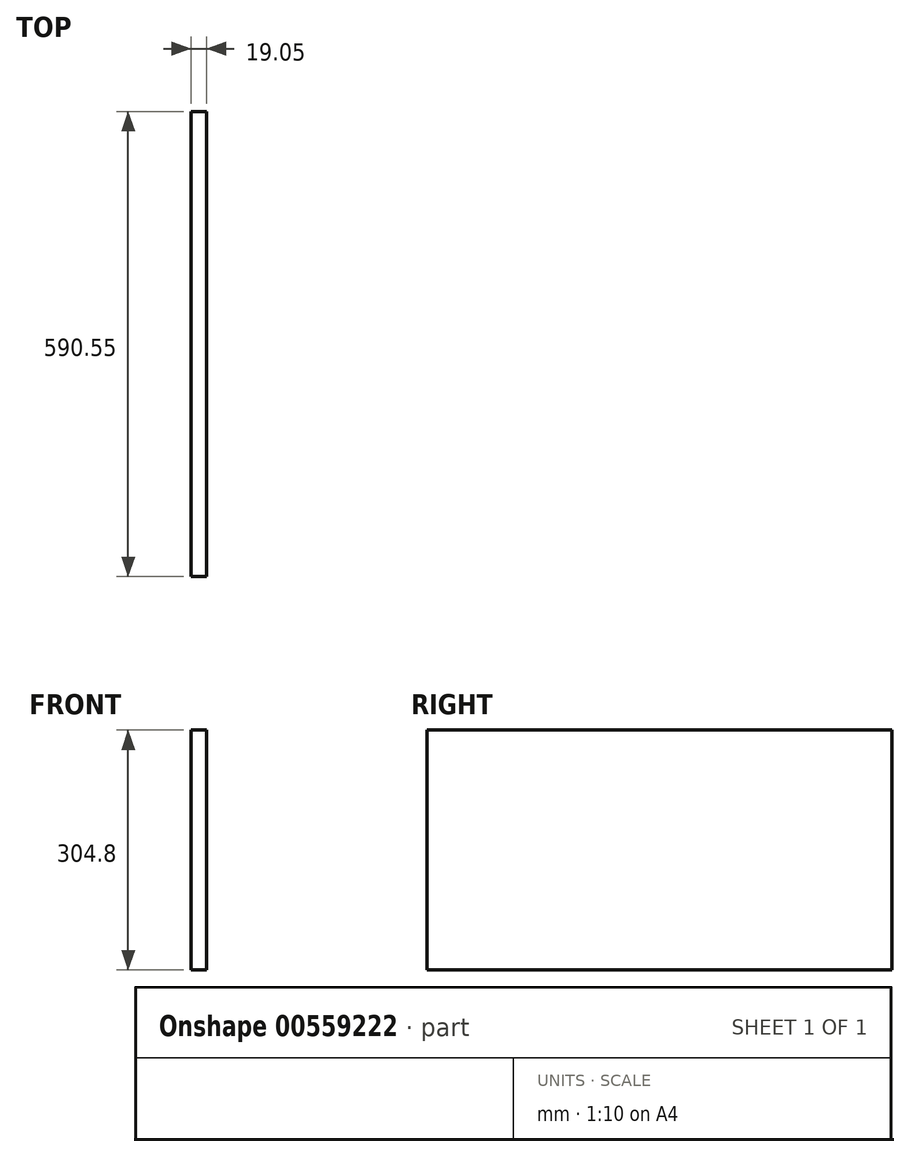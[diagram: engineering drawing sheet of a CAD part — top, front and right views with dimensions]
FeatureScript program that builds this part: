
annotation { "Feature Type Name" : "Feature", "Feature Type Description" : "" }
export const myFeature = defineFeature(function(context is Context, id is Id, definition is map)
    precondition{}
    {
        {
            var Q0;
            Q0=qCreatedBy(makeId("Right.planeOp"),FACE);
            var sketch = newSketch(context, id + "F0", { "sketchPlane" : qUnion([Q0])});
            skLineSegment(sketch, "E0.bottom", {"start": v(0, 0) * mm, "end": v(590.55, 0) * mm});
            skLineSegment(sketch, "E0.top", {"start": v(0, 304.8) * mm, "end": v(590.55, 304.8) * mm});
            skLineSegment(sketch, "E0.left", {"start": v(0, 0) * mm, "end": v(0, 304.8) * mm});
            skLineSegment(sketch, "E0.right", {"start": v(590.55, 0) * mm, "end": v(590.55, 304.8) * mm});
            skSolve(sketch);
        }
        {
            var Q0;
            Q0=makeQuery(id+"F0.imprint","IMPRINT",FACE,{"disambiguationData":[TD([[makeQuery(id+"F0.imprint","IMPRINT",EDGE,{"derivedFrom":sQuery(id+"F0.wireOp",EDGE,"E0.bottom")}),1.0]])]});
            extrude(context, id + "F1", {"entities" : qUnion([Q0]), "depth" : 19.05 * mm, "offsetDistance" : 25.4 * mm});
        }
    });
